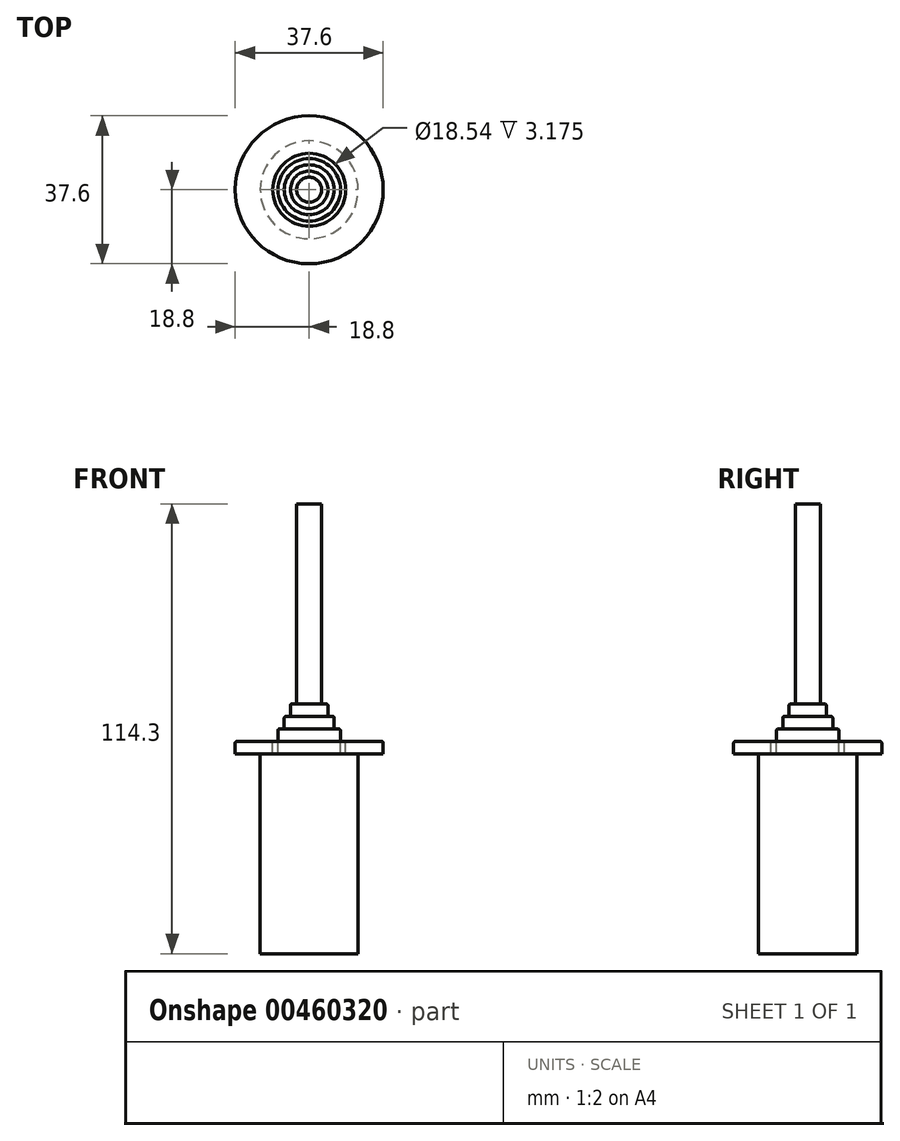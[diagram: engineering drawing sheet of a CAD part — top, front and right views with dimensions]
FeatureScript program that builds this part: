
annotation { "Feature Type Name" : "Feature", "Feature Type Description" : "" }
export const myFeature = defineFeature(function(context is Context, id is Id, definition is map)
    precondition{}
    {
        {
            var Q0;
            Q0=qCreatedBy(makeId("Front.planeOp"),FACE);
            var sketch = newSketch(context, id + "F0", { "sketchPlane" : qUnion([Q0])});
            skLineSegment(sketch, "E0", {"start": v(0, 0) * mm, "end": v(0, -50.8) * mm});
            skLineSegment(sketch, "E1", {"start": v(0, -50.8) * mm, "end": v(12.45, -50.8) * mm});
            skLineSegment(sketch, "E2", {"start": v(12.45, -50.8) * mm, "end": v(12.45, 0) * mm});
            skLineSegment(sketch, "E3", {"start": v(12.45, 0) * mm, "end": v(18.8, 0) * mm});
            skLineSegment(sketch, "E4", {"start": v(18.8, 0) * mm, "end": v(18.8, 2.7) * mm});
            skLineSegment(sketch, "E5", {"start": v(18.32, 3.18) * mm, "end": v(9.27, 3.18) * mm});
            skLineSegment(sketch, "E6", {"start": v(9.27, 3.17) * mm, "end": v(9.27, 0) * mm});
            skLineSegment(sketch, "E7", {"start": v(9.27, 0) * mm, "end": v(0, 0) * mm});
            skLineSegment(sketch, "E8", {"start": v(7.94, 0) * mm, "end": v(7.94, 5.88) * mm});
            skLineSegment(sketch, "E9", {"start": v(7.47, 6.35) * mm, "end": v(6.82, 6.35) * mm});
            skLineSegment(sketch, "E10", {"start": v(6.35, 6.82) * mm, "end": v(6.35, 9.05) * mm});
            skLineSegment(sketch, "E11", {"start": v(5.88, 9.53) * mm, "end": v(5.23, 9.53) * mm});
            skLineSegment(sketch, "E12", {"start": v(4.76, 10) * mm, "end": v(4.76, 12.23) * mm});
            skLineSegment(sketch, "E13", {"start": v(4.3, 12.7) * mm, "end": v(3.18, 12.7) * mm});
            skLineSegment(sketch, "E14", {"start": v(3.18, 12.7) * mm, "end": v(3.18, 63.5) * mm});
            skLineSegment(sketch, "E15", {"start": v(3.18, 63.5) * mm, "end": v(0, 63.5) * mm});
            skLineSegment(sketch, "E16", {"start": v(0, 63.5) * mm, "end": v(0, 0) * mm});
            skPoint(sketch, "E17.visualSharp", {"position": v(18.8, 3.18) * mm});
            skArc(sketch, "E17.filletArc", {"start": v(18.8, 2.7) * mm, "mid": v(18.66, 3.04) * mm, "end": v(18.32, 3.17) * mm});
            skPoint(sketch, "E18.visualSharp", {"position": v(7.94, 6.35) * mm});
            skArc(sketch, "E18.filletArc", {"start": v(7.94, 5.88) * mm, "mid": v(7.8, 6.21) * mm, "end": v(7.47, 6.35) * mm});
            skPoint(sketch, "E19.visualSharp", {"position": v(6.35, 6.35) * mm});
            skArc(sketch, "E19.filletArc", {"start": v(6.35, 6.82) * mm, "mid": v(6.49, 6.49) * mm, "end": v(6.82, 6.35) * mm});
            skPoint(sketch, "E20.visualSharp", {"position": v(6.35, 9.53) * mm});
            skArc(sketch, "E20.filletArc", {"start": v(6.35, 9.05) * mm, "mid": v(6.21, 9.39) * mm, "end": v(5.88, 9.53) * mm});
            skPoint(sketch, "E21.visualSharp", {"position": v(4.76, 9.53) * mm});
            skArc(sketch, "E21.filletArc", {"start": v(4.76, 10) * mm, "mid": v(4.9, 9.66) * mm, "end": v(5.23, 9.53) * mm});
            skPoint(sketch, "E22.visualSharp", {"position": v(4.76, 12.7) * mm});
            skArc(sketch, "E22.filletArc", {"start": v(4.76, 12.23) * mm, "mid": v(4.62, 12.56) * mm, "end": v(4.3, 12.7) * mm});
            skLineSegment(sketch, "E23", {"start": v(0, 78.82) * mm, "end": v(0, -66.17) * mm, "construction": true});
            skSolve(sketch);
        }
        {
            var Q0;
            Q0 = qSketchRegion(id + "F0", true);
            var Q1;
            Q1=sQuery(id+"F0.wireOp",EDGE,"E23");
            revolve(context, id + "F1", {"entities" : qUnion([Q0]), "axis" : qUnion([Q1]), "revolveType" : RevolveType.FULL});
        }
    });
